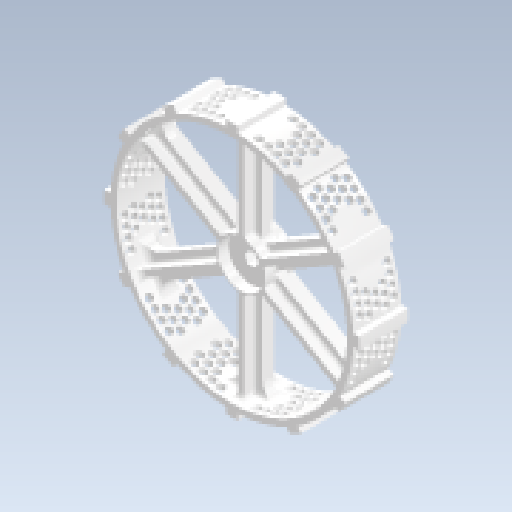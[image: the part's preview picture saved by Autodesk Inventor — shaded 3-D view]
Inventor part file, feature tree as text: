
AUTODESK INVENTOR PART (.ipt)
format: ipt  version: 2023 (Build 270158000, 158)  size: 1,789,952 bytes
history: native  units: in
note: dims shown in document units (in); Inventor stores cm internally (conversion verified against a paired STEP export)
features: extrude x7, fillet x7, sketch x7, pattern_circular x3, plane x2, mirror x1, projected_geometry x1
ambient origin geometry x8: Origin, YZ Plane, XZ Plane, XY Plane, X Axis, Y Axis, Z Axis, Center Point
bodies: Solid1 (feature_tree)
feature tree (28):
  extrude  "Extrusion1"  Depth=0.25in
  extrude  "Extrusion2"  Depth=2.0in
  extrude  "Extrusion4"  Depth=0.4375in
  extrude  "Extrusion5"  Depth=0.25in
  pattern_circular  "Circular Pattern1"  [2 undecoded]
  extrude  "Extrusion6"  Depth=2.3622in TaperAngle=360.0deg
  fillet  "Fillet9"  Radius=1.0in
  fillet  "Fillet10"  Radius=0.0625in
  fillet  "Fillet11"  Radius=0.5in
  fillet  "Fillet12"  Radius=0.25in
  fillet  "Fillet13"  Radius=0.125in
  fillet  "Fillet14"  Radius=0.125in
  fillet  "Fillet15"  Radius=0.25in
  extrude  "Extrusion7"  Depth=0.125in
  pattern_circular  "Circular Pattern2"  [2 undecoded]
  plane  "Work Plane1"
  extrude  "Extrusion8"  Depth=0.5in
  plane  "Work Plane2"
  mirror  "Mirror1"
  pattern_circular  "Circular Pattern3"  [2 undecoded]
  sketch  "Sketch1"  dims[d0=10.0in d1=0.25in]
  sketch  "Sketch2"  dims[d2=2.0in d3=0.0in d4=2.0in]
  sketch  "Sketch5"  dims[d6=0.875in d7=0.4375in]
  projected_geometry  "Projected Loop1"
  sketch  "Sketch6"  dims[d8=0.375in d9=0.0in d21=0.25in]
  sketch  "Sketch7"  dims[d22=0.125in]
  sketch  "Sketch8"  dims[d23=1.25in d24=0.0in]
  sketch  "Sketch11"  dims[d26=2.0in d27=1.25in d28=0.0in d31=2.3622in d32=360.0deg d35=1.0in d36=0.0in d43=0.0625in d44=0.5in d45=0.25in d46=0.125in d47=0.125in d48=0.25in d49=0.125in d50=0.125in d51=0.5in d52=0.25in d53=0.25in d54=0.0in d55=4.7244in d56=360.0deg d73=0.3125in d75=0.3125in d76=0.3125in d77=0.375in d78=0.375in d79=0.6005in d80=0.3125in d81=0.0in d82=0.35in d83=0.35in d84=0.35in d85=0.3125in d86=0.375in d87=0.3125in d88=0.35in d89=0.3125in d90=0.375in d91=0.5in d92=0.0in d93=0.4108in d94=0.35in d95=0.4156in d96=0.7906in d97=2.3622in d98=360.0deg d100=0.3125in d101=0.375in d102=0.3125in d103=0.375in d104=0.35in d105=0.35in d106=0.5in d29=0.0in d30=0.0in d37=0.5in d38=0.0344in d39=0.5in d40=0.0344in]
note: 6 required parameter values undecoded (feature->parameter linkage not recoverable at this tier; creation-order binding heuristic only, values carry confidence <= 0.55)
